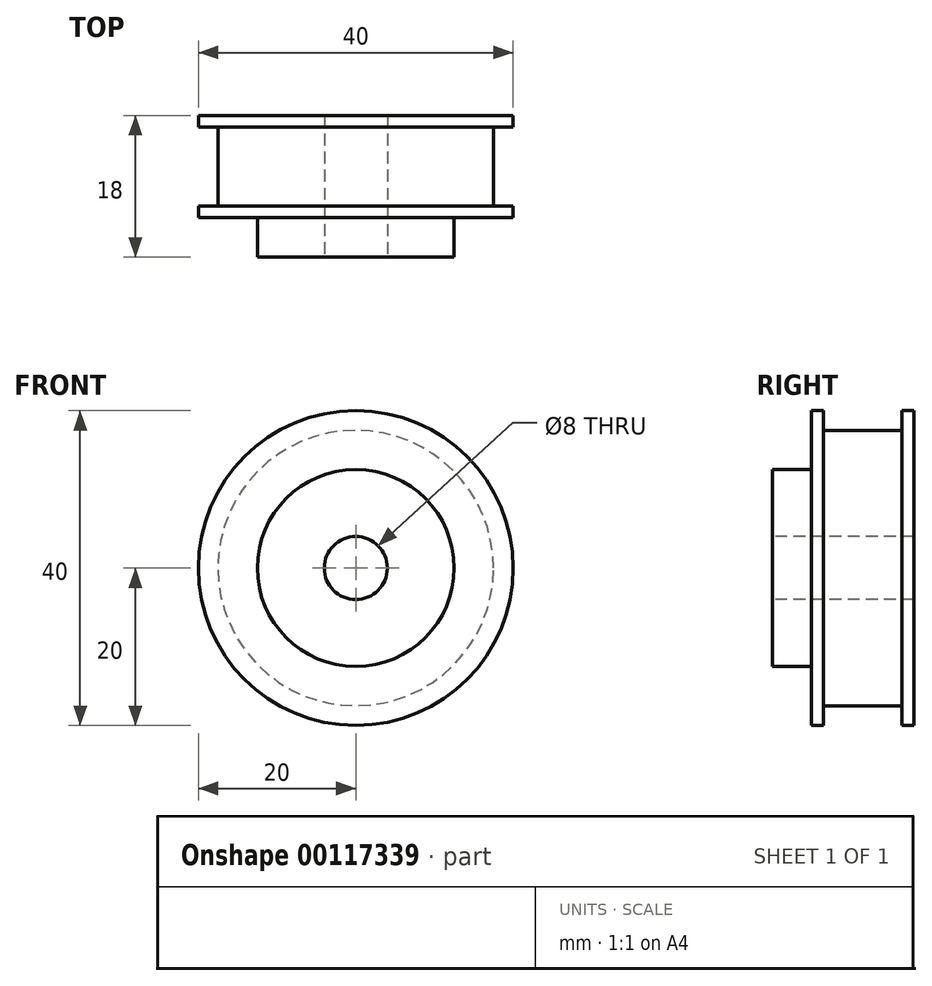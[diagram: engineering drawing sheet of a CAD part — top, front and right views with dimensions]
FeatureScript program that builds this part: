
annotation { "Feature Type Name" : "Feature", "Feature Type Description" : "" }
export const myFeature = defineFeature(function(context is Context, id is Id, definition is map)
    precondition{}
    {
        {
            var Q0;
            Q0=qCreatedBy(makeId("Front.planeOp"),FACE);
            var sketch = newSketch(context, id + "F0", { "sketchPlane" : qUnion([Q0])});
            skCircle(sketch, "E0", {"center": v(0, 0) * mm, "radius": 20 * mm});
            skSolve(sketch);
        }
        {
            var Q0;
            Q0=qSketchRegion(id+"F0",true);
            extrude(context, id + "F1", {"entities" : qUnion([Q0]), "depth" : 1.5 * mm});
        }
        {
            var Q0;
            Q0=makeQuery(id+"F1.opExtrude","CAP_FACE",FACE,{"disambiguationData":[OSD([sQuery(id+"F0.wireOp",EDGE,"E0")])],"isStart":false});
            var sketch = newSketch(context, id + "F2", { "sketchPlane" : qUnion([Q0])});
            skCircle(sketch, "E1", {"center": v(0, 0) * mm, "radius": 17.5 * mm});
            skSolve(sketch);
        }
        {
            var Q0;
            Q0=qSketchRegion(id+"F2",true);
            extrude(context, id + "F3", {"entities" : qUnion([Q0]), "operationType" : NewBodyOperationType.ADD, "depth" : 10 * mm});
        }
        {
            var Q0;
            Q0=makeQuery(id+"F3.opExtrude","CAP_FACE",FACE,{"disambiguationData":[OSD([sQuery(id+"F2.wireOp",EDGE,"E1")])],"isStart":false});
            var sketch = newSketch(context, id + "F4", { "sketchPlane" : qUnion([Q0])});
            skCircle(sketch, "E2", {"center": v(0, 0) * mm, "radius": 20 * mm});
            skSolve(sketch);
        }
        {
            var Q0;
            Q0=qSketchRegion(id+"F4",true);
            extrude(context, id + "F5", {"entities" : qUnion([Q0]), "operationType" : NewBodyOperationType.ADD, "depth" : 1.5 * mm});
        }
        {
            var Q0;
            Q0=makeQuery(id+"F5.opExtrude","CAP_FACE",FACE,{"disambiguationData":[OSD([sQuery(id+"F4.wireOp",EDGE,"E2")])],"isStart":false});
            var sketch = newSketch(context, id + "F6", { "sketchPlane" : qUnion([Q0])});
            skCircle(sketch, "E3", {"center": v(0, 0) * mm, "radius": 12.5 * mm});
            skSolve(sketch);
        }
        {
            var Q0;
            Q0=qSketchRegion(id+"F6",true);
            extrude(context, id + "F7", {"entities" : qUnion([Q0]), "operationType" : NewBodyOperationType.ADD, "depth" : 5 * mm});
        }
        {
            var Q0;
            Q0=makeQuery(id+"F7.opExtrude","CAP_FACE",FACE,{"disambiguationData":[OSD([sQuery(id+"F6.wireOp",EDGE,"E3")])],"isStart":false});
            var sketch = newSketch(context, id + "F8", { "sketchPlane" : qUnion([Q0])});
            skCircle(sketch, "E4", {"center": v(0, 0) * mm, "radius": 4 * mm});
            skSolve(sketch);
        }
        {
            var Q0;
            Q0=qSketchRegion(id+"F8",true);
            extrude(context, id + "F9", {"entities" : qUnion([Q0]), "operationType" : NewBodyOperationType.REMOVE, "oppositeDirection" : true, "depth" : 20 * mm});
        }
    });
